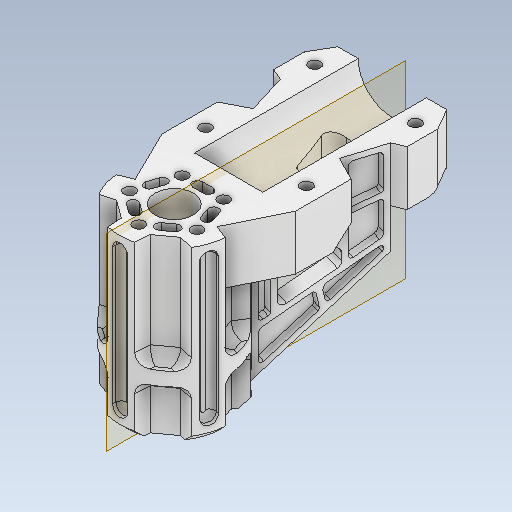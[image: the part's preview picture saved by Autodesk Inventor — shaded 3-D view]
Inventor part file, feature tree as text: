
AUTODESK INVENTOR PART (.ipt)
format: ipt  version: 2020 (Build 240168000, 168)  size: 1,578,496 bytes
history: native  units: mm
features: projected_geometry x35, sketch x27, extrude x24, fillet x14, thicken_offset x11, mirror x6, pattern_circular x4, chamfer x4, other x4, plane x3, revolve x2, reference x2, hole x1
ambient origin geometry x8: Origin, YZ Plane, XZ Plane, XY Plane, X Axis, Y Axis, Z Axis, Center Point
bodies: Solid1 (feature_tree)
feature tree (137):
  extrude  "Extrusion1"  Depth=12.0mm
  extrude  "Extrusion2"  Depth=18.0mm
  extrude  "Extrusion3"  Depth=20.0mm
  extrude  "Extrusion4"  Depth=60.0mm TaperAngle=0.0deg
  extrude  "Extrusion5"  Depth=45.0mm TaperAngle=0.0deg
  plane  "Work Plane1"
  revolve  "Revolution1"  [1 undecoded]
  extrude  "Extrusion6"  Depth=45.0mm TaperAngle=0.0deg
  pattern_circular  "Circular Pattern1"  Count=9  [1 undecoded]
  thicken_offset  "Thicken1"
  extrude  "Extrusion7"  Depth=2.0mm
  extrude  "Extrusion8"  Depth=90.0mm TaperAngle=0.0deg
  extrude  "Extrusion9"  Depth=50.0mm
  thicken_offset  "Thicken2"
  thicken_offset  "Thicken3"
  extrude  "Extrusion10"  Depth=4.2mm
  extrude  "Extrusion11"  Depth=125.0mm
  mirror  "Mirror1"
  thicken_offset  "Thicken4"
  thicken_offset  "Thicken5"
  revolve  "Revolution2"  [1 undecoded]
  fillet  "Fillet1"  Radius=2.0mm
  thicken_offset  "Thicken6"
  thicken_offset  "Thicken7"
  extrude  "Extrusion12"  Depth=2.0mm
  extrude  "Extrusion13"  Depth=40.0mm
  pattern_circular  "Circular Pattern2"  Count=9  [1 undecoded]
  extrude  "Extrusion14"  TaperAngle=30.0deg  [1 undecoded]
  extrude  "Extrusion15"  Depth=4.2mm
  extrude  "Extrusion16"  Depth=60.0mm TaperAngle=360.0deg
  mirror  "Mirror2"
  plane  "Work Plane2"
  extrude  "Extrusion17"  Depth=2.0mm
  chamfer  "Chamfer1"  Distance=2.0mm
  hole  "Hole1"  [1 undecoded]
  chamfer  "Chamfer2"  Distance=2.0mm
  chamfer  "Chamfer3"  Distance=12.0mm
  fillet  "Fillet3"  Radius=8.0mm
  fillet  "Fillet4"  Radius=20.0mm
  chamfer  "Chamfer5"  Angle=90.0deg  [1 undecoded]
  fillet  "Fillet5"  Radius=2.0mm
  thicken_offset  "Thicken8"
  thicken_offset  "Thicken9"
  thicken_offset  "Thicken10"
  thicken_offset  "Thicken11"
  extrude  "Extrusion18"  Depth=2.0mm
  extrude  "Extrusion19"  Depth=2.0mm
  extrude  "Extrusion20"  Depth=2.0mm
  extrude  "Extrusion21"  Depth=2.0mm
  pattern_circular  "Circular Pattern3"  [2 undecoded]
  mirror  "Mirror3"
  extrude  "Extrusion22"  Depth=8.0mm
  mirror  "Mirror4"
  extrude  "Extrusion23"  Depth=8.0mm
  mirror  "Mirror5"
  plane  "Work Plane3"
  extrude  "Extrusion24"  Depth=4.0mm
  pattern_circular  "Circular Pattern4"  [2 undecoded]
  fillet  "Fillet10"  Radius=20.0mm
  fillet  "Fillet11"  Radius=4.0mm
  fillet  "Fillet12"  Radius=4.0mm
  fillet  "Fillet13"  Radius=4.0mm
  fillet  "Fillet14"  Radius=22.68928mm
  fillet  "Fillet15"  Radius=22.68928mm
  mirror  "Mirror6"
  fillet  "Fillet16"  Radius=20.0mm
  fillet  "Fillet17"  Radius=40.0mm
  fillet  "Fillet18"  Radius=20.0mm
  fillet  "Fillet19"  Radius=20.0mm
  sketch  "Sketch1"  dims[d0=12.0mm d1=12.0mm]
  reference  "Reference1"
  sketch  "Sketch2"  dims[d2=18.0mm d3=18.0mm]
  projected_geometry  "Projected Loop1"
  sketch  "Sketch3"  dims[d4=60.0mm d5=0.0mm d6=20.0mm]
  projected_geometry  "Projected Loop2"
  sketch  "Sketch4"  dims[d7=40.0mm d8=60.0mm d9=0.0mm]
  projected_geometry  "Projected Loop3"
  projected_geometry  "Projected Loop4"
  sketch  "Sketch5"  dims[d10=40.0mm d11=45.0mm d12=0.0mm]
  projected_geometry  "Projected Loop5"
  projected_geometry  "Projected Loop6"
  sketch  "Sketch6"  dims[d13=45.0mm d14=0.0mm d15=8.0mm]
  projected_geometry  "Projected Loop7"
  projected_geometry  "Projected Loop8"
  projected_geometry  "Projected Loop9"
  sketch  "Sketch7"  dims[d16=8.0mm d17=45.0mm d18=0.0mm]
  projected_geometry  "Projected Loop10"
  sketch  "Sketch8"  dims[d19=7.0mm]
  projected_geometry  "Projected Loop11"
  sketch  "Sketch9"  dims[d20=35.0mm]
  projected_geometry  "Projected Loop12"
  sketch  "Sketch10"  dims[d21=45.0mm]
  projected_geometry  "Projected Loop13"
  projected_geometry  "Projected Loop14"
  projected_geometry  "Projected Loop15"
  projected_geometry  "Projected Loop16"
  projected_geometry  "Projected Loop17"
  sketch  "Sketch11"  dims[d22=90.0deg]
  projected_geometry  "Projected Loop18"
  sketch  "Sketch12"  dims[d23=13.0mm]
  projected_geometry  "Projected Loop19"
  sketch  "Sketch13"  dims[d24=4.2mm d25=90.0mm d26=0.0mm]
  projected_geometry  "Projected Loop20"
  projected_geometry  "Projected Loop21"
  sketch  "Sketch14"  dims[d27=50.0mm d28=360.0deg d30=2.0mm d31=4.0mm]
  projected_geometry  "Projected Loop22"
  sketch  "Sketch15"  dims[d32=14.0mm d33=90.0mm d34=0.0mm]
  projected_geometry  "Projected Loop23"
  sketch  "Sketch16"  dims[d35=50.0mm d36=50.0mm]
  projected_geometry  "Projected Loop24"
  projected_geometry  "Projected Loop25"
  sketch  "Sketch17"  dims[d37=4.2mm d38=4.2mm]
  projected_geometry  "Projected Loop26"
  sketch  "Sketch18"  dims[d39=90.0mm d40=0.0mm d41=125.0mm]
  projected_geometry  "Projected Loop27"
  sketch  "Sketch19"  dims[d42=90.0mm d43=0.0mm d44=2.0mm d45=2.0mm]
  projected_geometry  "Projected Loop28"
  sketch  "Sketch20"  dims[d46=2.0mm d47=2.0mm]
  projected_geometry  "Projected Loop29"
  reference  "Reference2"
  sketch  "Sketch21"  dims[d48=40.0mm d49=40.0mm]
  projected_geometry  "Projected Loop30"
  sketch  "Sketch22"  dims[d50=4.2mm]
  projected_geometry  "Projected Loop31"
  sketch  "Sketch23"  dims[d51=4.2mm d52=90.0mm d53=0.0mm]
  projected_geometry  "Projected Loop32"
  sketch  "Sketch24"  dims[d54=4.2mm d56=30.0deg]
  projected_geometry  "Projected Loop33"
  sketch  "Sketch27"  dims[d57=60.0mm d59=360.0deg d61=4.2mm]
  projected_geometry  "Projected Loop36"
  sketch  "Sketch28"  dims[d62=30.0deg d63=60.0mm d65=360.0deg]
  projected_geometry  "Projected Loop37"
  sketch  "Sketch29"  dims[d67=4.0mm d68=0.0mm d69=2.0mm d70=2.0mm d71=2.0mm d72=2.0mm d73=12.0mm d74=8.0mm d75=20.0mm d76=90.0deg d77=2.0mm d78=2.0mm d79=2.0mm d80=2.0mm d81=2.0mm d82=15.0mm d83=8.0mm d84=8.0mm d85=4.0mm d86=2.0mm d87=20.0mm d88=0.0mm d89=4.0mm d90=4.0mm d91=4.0mm d92=22.68928mm d93=22.68928mm d94=20.0mm d95=0.0mm d96=40.0mm d97=37.699112mm d99=20.0mm d100=0.0mm d101=20.0mm d102=0.0mm d103=22.68928mm d104=15.0mm d105=17.453293mm d106=20.0mm d107=0.0mm d108=40.0mm d109=5.0mm d110=0.0mm d111=6.0mm d112=2.0mm d113=45.0deg d114=4.2mm d115=6.0mm d116=4.0mm d117=2.0mm d118=90.0deg d119=5.0mm d120=0.0mm d121=4.5mm d122=2.0mm d123=60.0deg d124=4.5mm d125=2.0mm d126=60.0deg d128=2.0mm d129=4.0mm d130=4.0mm d134=3.0mm d135=2.0mm d136=60.0deg d137=2.0mm d138=1.0mm d139=1.0mm d140=1.0mm d141=1.0mm d142=1.0mm d143=1.0mm d144=1.0mm d145=1.0mm d146=32.0mm d147=5.585054mm d148=5.585054mm d149=12.0mm d150=0.0mm d152=2.0mm d153=2.0mm d154=2.0mm d155=2.0mm d156=3.0mm d157=3.0mm d158=4.0mm d159=0.0mm d160=46.0mm d161=2.0mm d163=2.0mm d164=2.0mm d165=2.0mm d166=2.5mm d167=10.0mm d168=0.0mm d169=2.0mm d170=3.5mm d171=80.0mm d172=0.0mm d173=50.0mm d174=360.0deg d181=2.0mm d182=2.0mm d183=2.0mm d184=2.0mm d185=2.0mm d186=2.0mm d187=2.0mm d188=2.0mm d189=2.0mm d190=2.0mm d191=2.0mm d192=2.0mm d193=2.0mm d194=2.0mm d195=2.0mm d196=2.0mm d197=2.0mm d198=3.0mm d199=0.0mm d203=6.0mm d204=2.0mm d205=5.0mm d206=2.0mm d207=3.0mm d208=0.0mm d211=25.0mm d212=5.5mm d213=5.5mm d214=0.0mm d215=30.0mm d216=25.132741mm d218=2.0mm d219=3.0mm d220=1.5mm d221=1.0mm d222=2.0mm d223=3.0mm d224=1.0mm d225=1.5mm d226=1.0mm d227=1.0mm d228=2.0mm d180=0.5mm]
  parser-record x1  (decoder bookkeeping rows leaked as tree rows — omitted from the tree; the rows remain in map.json)
  other  "sub_leg_1.iam"
  other  "carbon_fiber_25_21_300:1"
  other  "joint_connector_6:1"
note: 11 required parameter values undecoded (feature->parameter linkage not recoverable at this tier; creation-order binding heuristic only, values carry confidence <= 0.55)
note: 1 file-system path scrubbed to <path> (originals preserved in map.json)